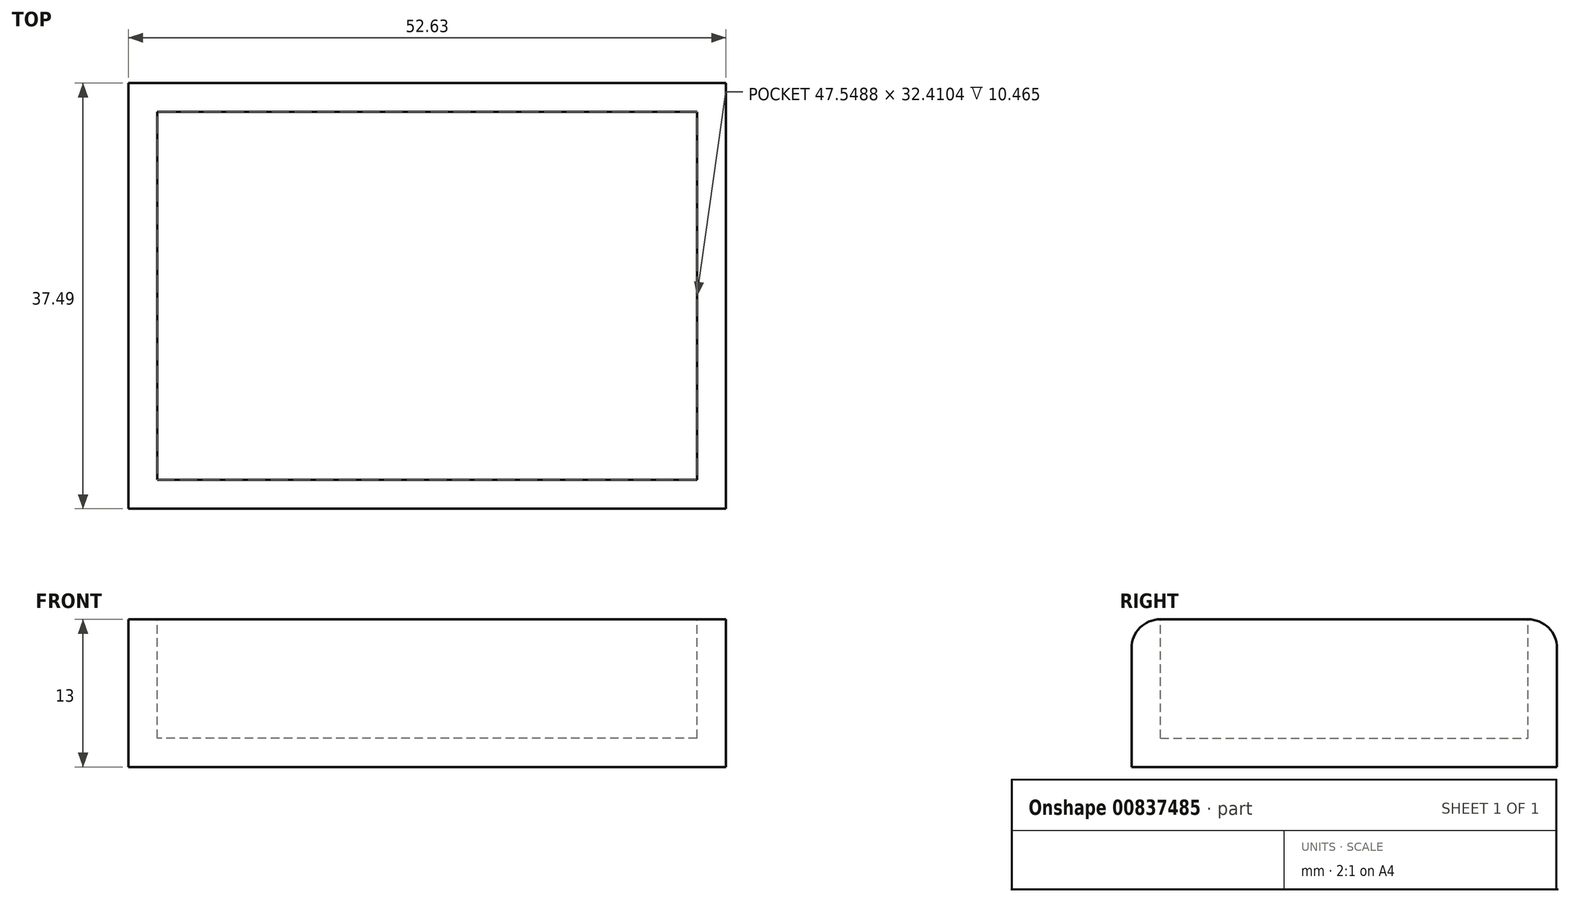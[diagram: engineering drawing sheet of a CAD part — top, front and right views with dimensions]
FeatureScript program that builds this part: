
annotation { "Feature Type Name" : "Feature", "Feature Type Description" : "" }
export const myFeature = defineFeature(function(context is Context, id is Id, definition is map)
    precondition{}
    {
        {
            var Q0;
            Q0=qCreatedBy(makeId("Right.planeOp"),FACE);
            var sketch = newSketch(context, id + "F0", { "sketchPlane" : qUnion([Q0])});
            skLineSegment(sketch, "E0.bottom", {"start": v(0, 0) * mm, "end": v(37.5, 0) * mm});
            skLineSegment(sketch, "E0.top", {"start": v(2.54, 13) * mm, "end": v(34.95, 13) * mm});
            skLineSegment(sketch, "E0.left", {"start": v(0, 0) * mm, "end": v(0, 10.46) * mm});
            skLineSegment(sketch, "E0.right", {"start": v(37.5, 0) * mm, "end": v(37.5, 10.46) * mm});
            skPoint(sketch, "E1.visualSharp", {"position": v(0, 13) * mm});
            skArc(sketch, "E1.filletArc", {"start": v(2.54, 13) * mm, "mid": v(0.74, 12.26) * mm, "end": v(0, 10.46) * mm});
            skPoint(sketch, "E2.visualSharp", {"position": v(37.5, 13) * mm});
            skArc(sketch, "E2.filletArc", {"start": v(37.5, 10.46) * mm, "mid": v(36.75, 12.26) * mm, "end": v(34.95, 13) * mm});
            skSolve(sketch);
        }
        {
            var Q0;
            Q0 = qSketchRegion(id + "F0", true);
            extrude(context, id + "F1", {"entities" : qUnion([Q0]), "depth" : 52.63 * mm, "offsetDistance" : 25.4 * mm});
        }
        {
            var Q0;
            Q0=makeQuery(id+"F1.opExtrude","SWEPT_FACE",FACE,{"disambiguationData":[OSD([sQuery(id+"F0.wireOp",EDGE,"E0.top")])]});
            var sketch = newSketch(context, id + "F2", { "sketchPlane" : qUnion([Q0])});
            skLineSegment(sketch, "E3", {"start": v(50.09, 2.54) * mm, "end": v(50.09, 34.95) * mm});
            skLineSegment(sketch, "E4", {"start": v(2.54, 2.54) * mm, "end": v(2.54, 34.95) * mm});
            skLineSegment(sketch, "E5", {"start": v(50.09, 2.54) * mm, "end": v(2.54, 2.54) * mm});
            skLineSegment(sketch, "E6", {"start": v(50.09, 34.95) * mm, "end": v(2.54, 34.95) * mm});
            skSolve(sketch);
        }
        {
            var Q0;
            Q0=makeQuery(id+"F1.opExtrude","SWEPT_FACE",FACE,{"disambiguationData":[OSD([sQuery(id+"F0.wireOp",EDGE,"E0.top")])]});
            shell(context, id + "F3", {"entities" : qUnion([Q0]), "thickness" : 2.54 * mm});
        }
        {
            var Q0;
            Q0 = qSketchRegion(id + "F2", true);
            extrude(context, id + "F4", {"entities" : qUnion([Q0]), "operationType" : NewBodyOperationType.REMOVE, "oppositeDirection" : true, "depth" : 2.54 * mm, "offsetDistance" : 25.4 * mm});
        }
    });
